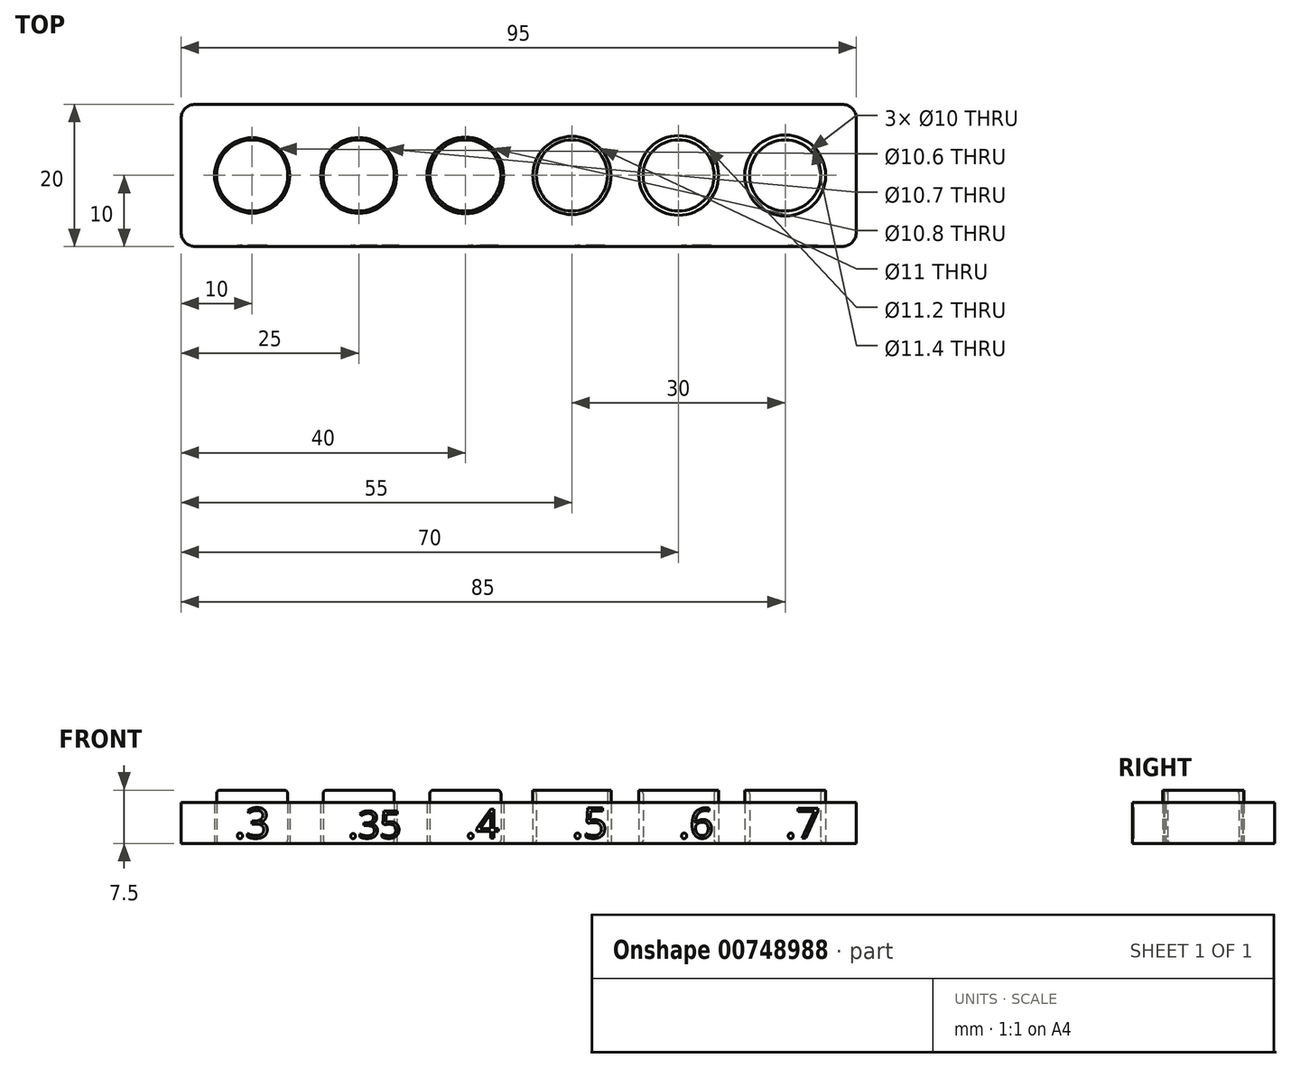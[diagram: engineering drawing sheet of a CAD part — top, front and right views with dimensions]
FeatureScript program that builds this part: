
annotation { "Feature Type Name" : "Feature", "Feature Type Description" : "" }
export const myFeature = defineFeature(function(context is Context, id is Id, definition is map)
    precondition{}
    {
        {
            var Q0;
            Q0=qCreatedBy(makeId("Top.planeOp"),FACE);
            var sketch = newSketch(context, id + "F0", { "sketchPlane" : qUnion([Q0])});
            skLineSegment(sketch, "E0.bottom", {"start": v(47.5, -10) * mm, "end": v(-47.5, -10) * mm});
            skLineSegment(sketch, "E0.top", {"start": v(47.5, 10) * mm, "end": v(-47.5, 10) * mm});
            skLineSegment(sketch, "E0.left", {"start": v(47.5, -10) * mm, "end": v(47.5, 10) * mm});
            skLineSegment(sketch, "E0.right", {"start": v(-47.5, -10) * mm, "end": v(-47.5, 10) * mm});
            skPoint(sketch, "E0.middle", {"position": v(0, 0) * mm});
            skLineSegment(sketch, "E1", {"start": v(-47.5, 0) * mm, "end": v(47.5, 0) * mm, "construction": true});
            skCircle(sketch, "E2", {"center": v(-37.5, 0) * mm, "radius": 5 * mm});
            skCircle(sketch, "E3", {"center": v(-22.5, 0) * mm, "radius": 5 * mm});
            skCircle(sketch, "E4", {"center": v(-7.5, 0) * mm, "radius": 5 * mm});
            skCircle(sketch, "E5.MirrorC", {"center": v(7.5, 0) * mm, "radius": 5 * mm});
            skCircle(sketch, "E6.MirrorC", {"center": v(22.5, 0) * mm, "radius": 5 * mm});
            skCircle(sketch, "E7.MirrorC", {"center": v(37.5, 0) * mm, "radius": 5 * mm});
            skCircle(sketch, "E8.0", {"center": v(-37.5, 0) * mm, "radius": 5.3 * mm});
            skCircle(sketch, "E9.0", {"center": v(-22.5, 0) * mm, "radius": 5.35 * mm});
            skCircle(sketch, "E10.0", {"center": v(-7.5, 0) * mm, "radius": 5.4 * mm});
            skCircle(sketch, "E11.0", {"center": v(7.5, 0) * mm, "radius": 5.5 * mm});
            skCircle(sketch, "E12.0", {"center": v(22.5, 0) * mm, "radius": 5.6 * mm});
            skCircle(sketch, "E13.0", {"center": v(37.5, 0) * mm, "radius": 5.7 * mm});
            skSolve(sketch);
        }
        {
            var Q0;
            Q0=makeQuery(id+"F0.imprint","IMPRINT",FACE,{"disambiguationData":[TD([[makeQuery(id+"F0.imprint","IMPRINT",EDGE,{"derivedFrom":sQuery(id+"F0.wireOp",EDGE,"E0.bottom")}),-1.0]])]});
            extrude(context, id + "F1", {"entities" : qUnion([Q0]), "depth" : 5.76 * mm, "offsetDistance" : 25 * mm});
        }
        {
            var Q0;
            Q0=makeQuery(id+"F0.imprint","IMPRINT",FACE,{"disambiguationData":[TD([[makeQuery(id+"F0.imprint","IMPRINT",EDGE,{"derivedFrom":sQuery(id+"F0.wireOp",EDGE,"E2")}),1.0]])]});
            var Q1;
            Q1=makeQuery(id+"F0.imprint","IMPRINT",FACE,{"disambiguationData":[TD([[makeQuery(id+"F0.imprint","IMPRINT",EDGE,{"derivedFrom":sQuery(id+"F0.wireOp",EDGE,"E3")}),1.0]])]});
            var Q2;
            Q2=makeQuery(id+"F0.imprint","IMPRINT",FACE,{"disambiguationData":[TD([[makeQuery(id+"F0.imprint","IMPRINT",EDGE,{"derivedFrom":sQuery(id+"F0.wireOp",EDGE,"E4")}),1.0]])]});
            var Q3;
            Q3=makeQuery(id+"F0.imprint","IMPRINT",FACE,{"disambiguationData":[TD([[makeQuery(id+"F0.imprint","IMPRINT",EDGE,{"derivedFrom":sQuery(id+"F0.wireOp",EDGE,"E5.MirrorC")}),-1.0]])]});
            var Q4;
            Q4=makeQuery(id+"F0.imprint","IMPRINT",FACE,{"disambiguationData":[TD([[makeQuery(id+"F0.imprint","IMPRINT",EDGE,{"derivedFrom":sQuery(id+"F0.wireOp",EDGE,"E6.MirrorC")}),-1.0]])]});
            var Q5;
            Q5=makeQuery(id+"F0.imprint","IMPRINT",FACE,{"disambiguationData":[TD([[makeQuery(id+"F0.imprint","IMPRINT",EDGE,{"derivedFrom":sQuery(id+"F0.wireOp",EDGE,"E7.MirrorC")}),-1.0]])]});
            extrude(context, id + "F2", {"entities" : qUnion([Q0, Q1, Q2, Q3, Q4, Q5]), "depth" : 7.5 * mm, "offsetDistance" : 25 * mm});
        }
        {
            var Q0;
            Q0=makeQuery(id+"F1.opExtrude","SWEPT_FACE",FACE,{"disambiguationData":[OSD([sQuery(id+"F0.wireOp",EDGE,"E0.bottom")])]});
            var sketch = newSketch(context, id + "F3", { "sketchPlane" : qUnion([Q0])});
            skText(sketch, "E14", { "text": ".3", "fontName": "OpenSans-Regular.ttf"});
            skText(sketch, "E15", { "text": ".35", "fontName": "OpenSans-Regular.ttf"});
            skText(sketch, "E16", { "text": ".4", "fontName": "OpenSans-Regular.ttf"});
            skText(sketch, "E17", { "text": ".5", "fontName": "OpenSans-Regular.ttf"});
            skText(sketch, "E18", { "text": ".6", "fontName": "OpenSans-Regular.ttf"});
            skText(sketch, "E19", { "text": ".7", "fontName": "OpenSans-Regular.ttf"});
            const initialGuessF3  = {"E14": [-0.04, 0.00076, 1, 0, 0.00427], "E15": [-0.024, 0.00076, 1, 0, 0.00381], "E16": [-0.0075, 0.00076, 1, 0, 0.00408], "E17": [0.0075, 0.00076, 1, 0, 0.00426], "E18": [0.0225, 0.00076, 1, 0, 0.00422], "E19": [0.0375, 0.00076, 1, 0, 0.00423]};
            skSetInitialGuess(sketch, initialGuessF3);
            skSolve(sketch);
        }
        {
            var Q0;
            Q0=qSketchRegion(id+"F3",true);
            extrude(context, id + "F4", {"entities" : qUnion([Q0]), "operationType" : NewBodyOperationType.REMOVE, "oppositeDirection" : true, "depth" : 0.2 * mm, "offsetDistance" : 25 * mm});
        }
        {
            var Q0;
            Q0=makeQuery(id+"F2.opExtrude","CAP_EDGE",EDGE,{"disambiguationData":[OSD([sQuery(id+"F0.wireOp",EDGE,"E2")])],"isStart":false});
            var Q1;
            Q1=makeQuery(id+"F2.opExtrude","CAP_EDGE",EDGE,{"disambiguationData":[OSD([sQuery(id+"F0.wireOp",EDGE,"E3")])],"isStart":false});
            var Q2;
            Q2=makeQuery(id+"F2.opExtrude","CAP_EDGE",EDGE,{"disambiguationData":[OSD([sQuery(id+"F0.wireOp",EDGE,"E4")])],"isStart":false});
            var Q3;
            Q3=makeQuery(id+"F2.opExtrude","CAP_EDGE",EDGE,{"disambiguationData":[OSD([sQuery(id+"F0.wireOp",EDGE,"E5.MirrorC")])],"isStart":false});
            var Q4;
            Q4=makeQuery(id+"F2.opExtrude","CAP_EDGE",EDGE,{"disambiguationData":[OSD([sQuery(id+"F0.wireOp",EDGE,"E6.MirrorC")])],"isStart":false});
            var Q5;
            Q5=makeQuery(id+"F2.opExtrude","CAP_EDGE",EDGE,{"disambiguationData":[OSD([sQuery(id+"F0.wireOp",EDGE,"E7.MirrorC")])],"isStart":false});
            var Q6;
            Q6=makeQuery(id+"F2.opExtrude","CAP_EDGE",EDGE,{"disambiguationData":[OSD([sQuery(id+"F0.wireOp",EDGE,"E2")])],"isStart":true});
            var Q7;
            Q7=makeQuery(id+"F2.opExtrude","CAP_EDGE",EDGE,{"disambiguationData":[OSD([sQuery(id+"F0.wireOp",EDGE,"E3")])],"isStart":true});
            var Q8;
            Q8=makeQuery(id+"F2.opExtrude","CAP_EDGE",EDGE,{"disambiguationData":[OSD([sQuery(id+"F0.wireOp",EDGE,"E4")])],"isStart":true});
            var Q9;
            Q9=makeQuery(id+"F2.opExtrude","CAP_EDGE",EDGE,{"disambiguationData":[OSD([sQuery(id+"F0.wireOp",EDGE,"E5.MirrorC")])],"isStart":true});
            var Q10;
            Q10=makeQuery(id+"F2.opExtrude","CAP_EDGE",EDGE,{"disambiguationData":[OSD([sQuery(id+"F0.wireOp",EDGE,"E6.MirrorC")])],"isStart":true});
            var Q11;
            Q11=makeQuery(id+"F2.opExtrude","CAP_EDGE",EDGE,{"disambiguationData":[OSD([sQuery(id+"F0.wireOp",EDGE,"E7.MirrorC")])],"isStart":true});
            fillet(context, id + "F5", {"entities" : qUnion([Q0, Q1, Q2, Q3, Q4, Q5, Q6, Q7, Q8, Q9, Q10, Q11]), "radius" : 0.5 * mm, "tangentPropagation" : true, "allowEdgeOverflow" : false});
        }
        {
            var Q0;
            Q0=makeQuery(id+"F1.opExtrude","SWEPT_EDGE",EDGE,{"disambiguationData":[OSD([sQuery(id+"F0.wireOp",EDGE,"E0.top"),sQuery(id+"F0.wireOp",EDGE,"E0.left")])]});
            var Q1;
            Q1=makeQuery(id+"F1.opExtrude","SWEPT_EDGE",EDGE,{"disambiguationData":[OSD([sQuery(id+"F0.wireOp",EDGE,"E0.bottom"),sQuery(id+"F0.wireOp",EDGE,"E0.left")])]});
            var Q2;
            Q2=makeQuery(id+"F1.opExtrude","SWEPT_EDGE",EDGE,{"disambiguationData":[OSD([sQuery(id+"F0.wireOp",EDGE,"E0.bottom"),sQuery(id+"F0.wireOp",EDGE,"E0.right")])]});
            var Q3;
            Q3=makeQuery(id+"F1.opExtrude","SWEPT_EDGE",EDGE,{"disambiguationData":[OSD([sQuery(id+"F0.wireOp",EDGE,"E0.top"),sQuery(id+"F0.wireOp",EDGE,"E0.right")])]});
            fillet(context, id + "F6", {"entities" : qUnion([Q0, Q1, Q2, Q3]), "radius" : 2 * mm, "tangentPropagation" : true, "allowEdgeOverflow" : false});
        }
    });
